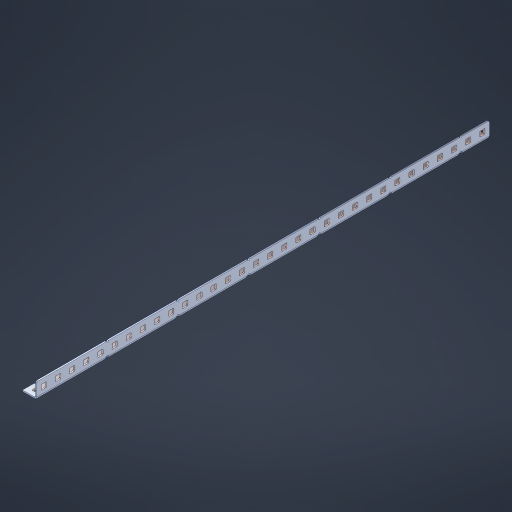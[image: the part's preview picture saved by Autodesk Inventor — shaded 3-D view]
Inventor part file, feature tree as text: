
AUTODESK INVENTOR PART (.ipt)
format: ipt  version: 2023 (Build 270158000, 158)  size: 1,270,272 bytes
history: native  units: in
note: dims shown in document units (in); Inventor stores cm internally (conversion verified against a paired STEP export)
features: other x103, extrude x94, sheet_metal_op x11, sketch x10, pattern_linear x2, mirror x1, chamfer x1
ambient origin geometry x8: Origin, YZ Plane, XZ Plane, XY Plane, X Axis, Y Axis, Z Axis, Center Point
bodies: Solid1 (feature_tree), Body (feature_tree)
feature tree (222):
  sheet_metal_op  "Flanges"
  other  "Flange Pattern Plane"
  other  "Flange Pattern Sketch"
  sheet_metal_op  "Flange Pattern"
  sheet_metal_op  "Body Pattern"
  pattern_linear  "Center Pattern"  Spacing1=0.0469in  [1 undecoded]
  other  "Arc Length"
  mirror  "Notch Mirror"
  pattern_linear  "Notch Pattern"  Spacing1=0.182in  [1 undecoded]
  chamfer  "End Chamfer"
  extrude  "Half Cut"  Depth=0.02in
  sketch  "Sketch1"  dims[d0=1.0in]
  other  "Plate1"
  sketch  "Sketch2"  dims[d1=16.0in]
  other  "Plate2"
  sheet_metal_op  "Bend1"
  sheet_metal_op  "Corner1"
  sketch  "Sketch3"  dims[d2=0.0469in]
  sketch  "Sketch7"  dims[d3=0.0469in]
  other  "Srf1"
  other  "Srf2"
  sketch  "Sketch8"  dims[d4=0.0234in]
  sketch  "Sketch9"  dims[d5=0.0938in]
  other  "Srf91"
  sheet_metal_op  "Body Pattern Sketch"
  other  "Srf92"
  sketch  "Sketch13"  dims[d6=0.0469in]
  sketch  "Sketch14"  dims[d7=0.5in d8=90.0deg d9=0.0312in]
  sketch  "Sketch15"  dims[d10=0.1875in]
  sketch  "Sketch16"  dims[d11=0.0469in d12=0.0469in d16=0.182in d17=0.02in d18=0.0469in d19=0.0in d20=0.25in d21=0.25in d38=12.5984in d40=0.5in d41=0.3937in d43=1.0in d46=0.172in d47=1.0in d48=0.0in d49=0.182in d50=0.02in d51=0.25in d52=0.25in d53=0.0469in d54=0.0in d55=0.172in d56=1.0in d57=0.0in d58=0.25in d60=12.5984in d62=0.5in d63=0.3937in d65=0.5in d85=0.1227in d86=0.1659in d88=0.04in d89=0.0469in d90=0.0in d91=0.04in d92=0.0491in d95=2.5in d96=0.04in d97=0.25in d98=45.0deg d99=0.25in d100=0.5in d101=0.0in d102=2.497in d106=0.182in d107=0.02in d108=0.5in d109=0.5in d110=0.0469in d111=0.0in d112=0.172in d113=0.5in d114=0.0in d117=0.5in d118=0.5in d119=0.5in]
  other  "Srf786"
  other  "Srf823"
  other  "Srf824"
  other  "Srf825"
  other  "Srf826"
  other  "Srf827"
  other  "Srf828"
  other  "Srf829"
  other  "Srf856"
  other  "Srf857"
  other  "Srf858"
  other  "Srf859"
  other  "Srf860"
  other  "Srf861"
  other  "Srf862"
  other  "Srf889"
  other  "Srf890"
  other  "Srf891"
  other  "Srf892"
  other  "Srf893"
  other  "Srf894"
  other  "Srf895"
  other  "Srf896"
  other  "Srf922"
  other  "Srf923"
  other  "Srf924"
  other  "Srf925"
  other  "Srf926"
  other  "Srf959"
  other  "Srf960"
  other  "Srf961"
  other  "Srf962"
  other  "Srf963"
  other  "Srf996"
  other  "Srf997"
  other  "Srf998"
  other  "Srf999"
  other  "Srf1000"
  other  "Srf1143"
  other  "Srf1144"
  other  "Srf1145"
  other  "Srf1146"
  other  "Srf1147"
  other  "Srf1148"
  other  "Srf1149"
  other  "Srf1150"
  other  "Srf1151"
  other  "Srf1152"
  other  "Srf1153"
  other  "Srf1154"
  other  "Srf1155"
  other  "Srf1156"
  other  "Srf1157"
  other  "Srf1158"
  other  "Srf1159"
  other  "Srf1160"
  other  "Srf1199"
  other  "Srf1200"
  other  "Srf1201"
  other  "Srf1202"
  other  "Srf1203"
  other  "Srf1204"
  other  "Srf1205"
  other  "Srf1206"
  other  "Srf1207"
  other  "Srf1208"
  other  "Srf1209"
  other  "Srf1210"
  other  "Srf1211"
  other  "Srf1212"
  other  "Srf1213"
  other  "Srf1214"
  other  "Srf1215"
  other  "Srf1216"
  other  "Srf1255"
  other  "Srf1256"
  other  "Srf1257"
  other  "Srf1258"
  other  "Srf1259"
  other  "Srf1260"
  other  "Srf1261"
  other  "Srf1262"
  other  "Srf1263"
  other  "Srf1264"
  other  "Srf1265"
  other  "Srf1266"
  other  "Srf1267"
  other  "Srf1268"
  other  "Srf1269"
  other  "Srf1270"
  other  "Srf1271"
  other  "Srf1272"
  sheet_metal_op  "Flange Stamp"
  sheet_metal_op  "Flange Circle"
  sheet_metal_op  "Body Stamp"
  sheet_metal_op  "Body Circle"
  other  "Center Stamp"
  other  "Center Circle"
  sheet_metal_op  "Notch"
  extrude  "ExtrusionSrf2"  Depth=0.0469in
  extrude  "ExtrusionSrf92"  TaperAngle=0.0deg  [1 undecoded]
  extrude  "ExtrusionSrf823"  Depth=0.25in
  extrude  "ExtrusionSrf824"  Depth=0.25in
  extrude  "ExtrusionSrf825"  Depth=0.5in
  extrude  "ExtrusionSrf826"  Depth=0.5in
  extrude  "ExtrusionSrf827"  Depth=1.0in TaperAngle=0.0deg
  extrude  "ExtrusionSrf828"  Depth=0.182in
  extrude  "ExtrusionSrf829"  Depth=0.02in
  extrude  "ExtrusionSrf856"  Depth=0.25in
  extrude  "ExtrusionSrf857"  Depth=0.25in
  extrude  "ExtrusionSrf858"  Depth=0.0469in
  extrude  "ExtrusionSrf859"  TaperAngle=0.0deg  [1 undecoded]
  extrude  "ExtrusionSrf860"  Depth=0.5in
  extrude  "ExtrusionSrf861"  Depth=1.0in TaperAngle=0.0deg
  extrude  "ExtrusionSrf862"  Depth=0.25in
  extrude  "ExtrusionSrf889"  Depth=0.5in
  extrude  "ExtrusionSrf890"  Depth=0.5in
  extrude  "ExtrusionSrf891"  Depth=0.5in
  extrude  "ExtrusionSrf892"  Depth=0.5in
  extrude  "ExtrusionSrf893"  Depth=0.5in
  extrude  "ExtrusionSrf894"  Depth=0.0469in
  extrude  "ExtrusionSrf895"  TaperAngle=0.0deg  [1 undecoded]
  extrude  "ExtrusionSrf896"  Depth=0.5in
  extrude  "ExtrusionSrf922"  Depth=0.5in
  extrude  "ExtrusionSrf923"  Depth=2.5in
  extrude  "ExtrusionSrf924"  Depth=0.25in TaperAngle=45.0deg
  extrude  "ExtrusionSrf925"  Depth=0.25in
  extrude  "ExtrusionSrf926"  Depth=0.5in TaperAngle=0.0deg
  extrude  "ExtrusionSrf959"  Depth=0.5in
  extrude  "ExtrusionSrf960"  Depth=0.182in
  extrude  "ExtrusionSrf961"  Depth=0.02in
  extrude  "ExtrusionSrf962"  Depth=0.5in
  extrude  "ExtrusionSrf963"  Depth=0.5in
  extrude  "ExtrusionSrf996"  Depth=0.0469in
  extrude  "ExtrusionSrf997"  TaperAngle=0.0deg  [1 undecoded]
  extrude  "ExtrusionSrf998"  Depth=0.5in
  extrude  "ExtrusionSrf999"  Depth=0.5in TaperAngle=0.0deg
  extrude  "ExtrusionSrf1000"  Depth=0.5in
  extrude  "ExtrusionSrf1143"  Depth=0.5in
  extrude  "ExtrusionSrf1144"  Depth=0.5in
  extrude  "ExtrusionSrf1145"  [1 undecoded]
  extrude  "ExtrusionSrf1146"  [1 undecoded]
  extrude  "ExtrusionSrf1147"  [1 undecoded]
  extrude  "ExtrusionSrf1148"  [1 undecoded]
  extrude  "ExtrusionSrf1149"  [1 undecoded]
  extrude  "ExtrusionSrf1150"  [1 undecoded]
  extrude  "ExtrusionSrf1151"  [1 undecoded]
  extrude  "ExtrusionSrf1152"  [1 undecoded]
  extrude  "ExtrusionSrf1153"  [1 undecoded]
  extrude  "ExtrusionSrf1154"  [1 undecoded]
  extrude  "ExtrusionSrf1155"  [1 undecoded]
  extrude  "ExtrusionSrf1156"  [1 undecoded]
  extrude  "ExtrusionSrf1157"  [1 undecoded]
  extrude  "ExtrusionSrf1158"  [1 undecoded]
  extrude  "ExtrusionSrf1159"  [1 undecoded]
  extrude  "ExtrusionSrf1160"  [1 undecoded]
  extrude  "ExtrusionSrf1199"  [1 undecoded]
  extrude  "ExtrusionSrf1200"  [1 undecoded]
  extrude  "ExtrusionSrf1201"  [1 undecoded]
  extrude  "ExtrusionSrf1202"  [1 undecoded]
  extrude  "ExtrusionSrf1203"  [1 undecoded]
  extrude  "ExtrusionSrf1204"  [1 undecoded]
  extrude  "ExtrusionSrf1205"  [1 undecoded]
  extrude  "ExtrusionSrf1206"  [1 undecoded]
  extrude  "ExtrusionSrf1207"  [1 undecoded]
  extrude  "ExtrusionSrf1208"  [1 undecoded]
  extrude  "ExtrusionSrf1209"  [1 undecoded]
  extrude  "ExtrusionSrf1210"  [1 undecoded]
  extrude  "ExtrusionSrf1211"  [1 undecoded]
  extrude  "ExtrusionSrf1212"  [1 undecoded]
  extrude  "ExtrusionSrf1213"  [1 undecoded]
  extrude  "ExtrusionSrf1214"  [1 undecoded]
  extrude  "ExtrusionSrf1215"  [1 undecoded]
  extrude  "ExtrusionSrf1216"  [1 undecoded]
  extrude  "ExtrusionSrf1255"  [1 undecoded]
  extrude  "ExtrusionSrf1256"  [1 undecoded]
  extrude  "ExtrusionSrf1257"  [1 undecoded]
  extrude  "ExtrusionSrf1258"  [1 undecoded]
  extrude  "ExtrusionSrf1259"  [1 undecoded]
  extrude  "ExtrusionSrf1260"  [1 undecoded]
  extrude  "ExtrusionSrf1261"  [1 undecoded]
  extrude  "ExtrusionSrf1262"  [1 undecoded]
  extrude  "ExtrusionSrf1263"  [1 undecoded]
  extrude  "ExtrusionSrf1264"  [1 undecoded]
  extrude  "ExtrusionSrf1265"  [1 undecoded]
  extrude  "ExtrusionSrf1266"  [1 undecoded]
  extrude  "ExtrusionSrf1267"  [1 undecoded]
  extrude  "ExtrusionSrf1268"  [1 undecoded]
  extrude  "ExtrusionSrf1269"  [1 undecoded]
  extrude  "ExtrusionSrf1270"  [1 undecoded]
  extrude  "ExtrusionSrf1271"  [1 undecoded]
  extrude  "ExtrusionSrf1272"  [1 undecoded]
note: 58 required parameter values undecoded (feature->parameter linkage not recoverable at this tier; creation-order binding heuristic only, values carry confidence <= 0.55)
